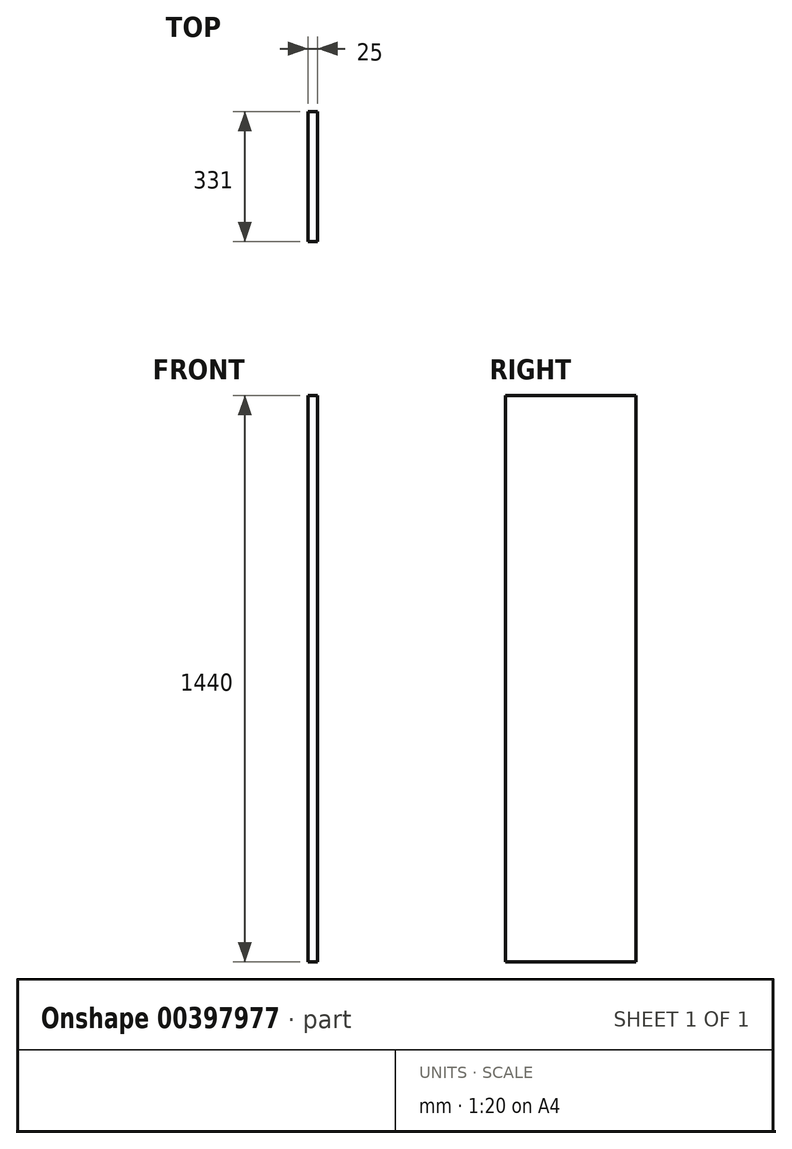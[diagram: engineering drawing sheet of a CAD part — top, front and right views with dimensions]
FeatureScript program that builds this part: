
annotation { "Feature Type Name" : "Feature", "Feature Type Description" : "" }
export const myFeature = defineFeature(function(context is Context, id is Id, definition is map)
    precondition{}
    {
        {
            var Q0;
            Q0=qCreatedBy(makeId("Right.planeOp"),FACE);
            var sketch = newSketch(context, id + "F0", { "sketchPlane" : qUnion([Q0])});
            skLineSegment(sketch, "E0.bottom", {"start": v(-165.5, 720) * mm, "end": v(165.5, 720) * mm});
            skLineSegment(sketch, "E0.top", {"start": v(-165.5, -720) * mm, "end": v(165.5, -720) * mm});
            skLineSegment(sketch, "E0.left", {"start": v(-165.5, 720) * mm, "end": v(-165.5, -720) * mm});
            skLineSegment(sketch, "E0.right", {"start": v(165.5, 720) * mm, "end": v(165.5, -720) * mm});
            skLineSegment(sketch, "E1", {"start": v(-165.5, 0) * mm, "end": v(165.5, 0) * mm, "construction": true});
            skSolve(sketch);
        }
        {
            var Q0;
            Q0 = qSketchRegion(id + "F0", true);
            extrude(context, id + "F1", {"entities" : qUnion([Q0]), "depth" : 25 * mm});
        }
    });
